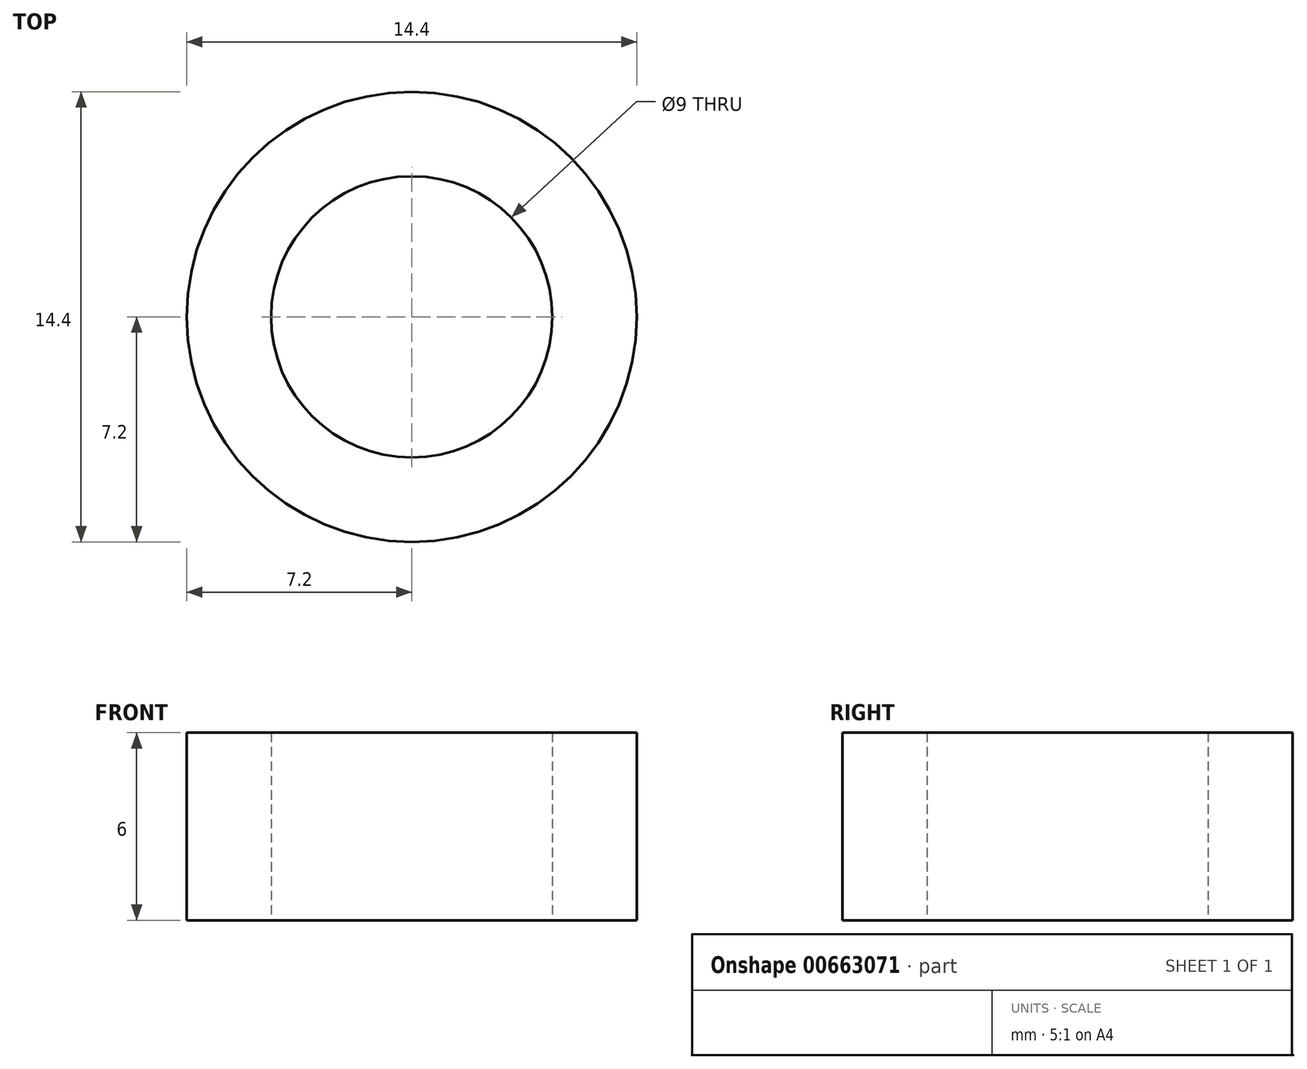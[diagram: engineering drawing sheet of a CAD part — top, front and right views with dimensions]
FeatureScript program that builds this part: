
annotation { "Feature Type Name" : "Feature", "Feature Type Description" : "" }
export const myFeature = defineFeature(function(context is Context, id is Id, definition is map)
    precondition{}
    {
        {
            var Q0;
            Q0=qCreatedBy(makeId("Top.planeOp"),FACE);
            var sketch = newSketch(context, id + "F0", { "sketchPlane" : qUnion([Q0])});
            skCircle(sketch, "E0", {"center": v(0, 0) * mm, "radius": 7.2 * mm});
            skSolve(sketch);
        }
        {
            var Q0;
            Q0=qSketchRegion(id+"F0",true);
            extrude(context, id + "F1", {"entities" : qUnion([Q0]), "depth" : 6 * mm, "offsetDistance" : 25.4 * mm});
        }
        {
            var Q0;
            Q0=qCreatedBy(makeId("Top.planeOp"),FACE);
            var sketch = newSketch(context, id + "F2", { "sketchPlane" : qUnion([Q0])});
            skCircle(sketch, "E1", {"center": v(0, 0) * mm, "radius": 4.5 * mm});
            skSolve(sketch);
        }
        {
            var Q0;
            Q0=qSketchRegion(id+"F2",true);
            extrude(context, id + "F3", {"entities" : qUnion([Q0]), "operationType" : NewBodyOperationType.REMOVE, "depth" : 6 * mm, "offsetDistance" : 25.4 * mm});
        }
    });
